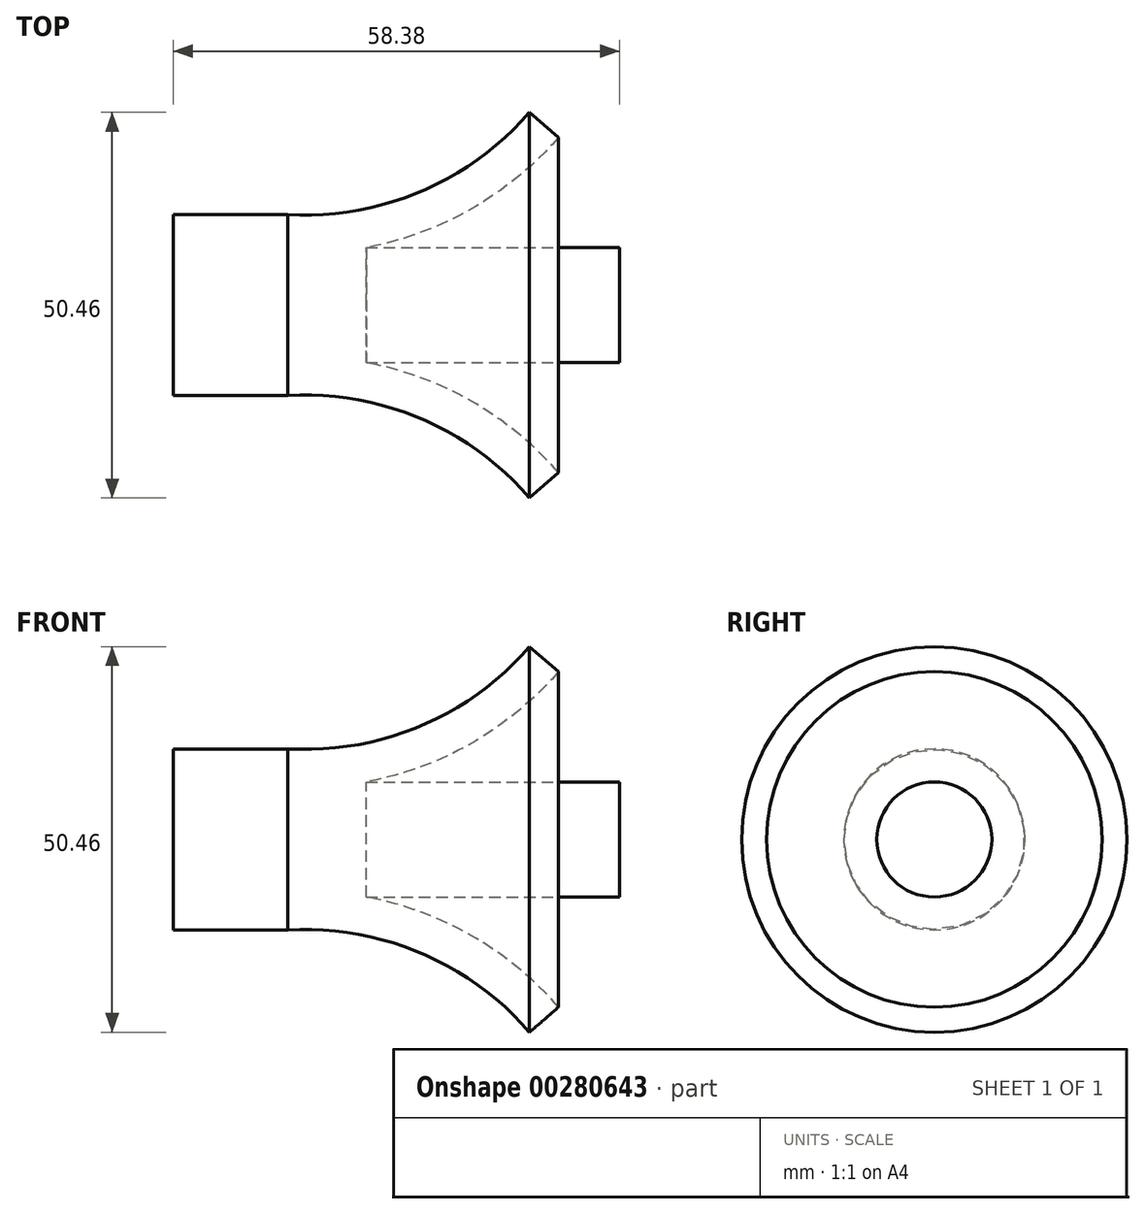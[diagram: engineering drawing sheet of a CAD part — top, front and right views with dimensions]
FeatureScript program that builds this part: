
annotation { "Feature Type Name" : "Feature", "Feature Type Description" : "" }
export const myFeature = defineFeature(function(context is Context, id is Id, definition is map)
    precondition{}
    {
        {
            var Q0;
            Q0=qCreatedBy(makeId("Top.planeOp"),FACE);
            var sketch = newSketch(context, id + "F0", { "sketchPlane" : qUnion([Q0])});
            skLineSegment(sketch, "E0", {"start": v(0, 0) * mm, "end": v(0, 11.86) * mm});
            skArc(sketch, "E1", {"start": v(0, 11.86) * mm, "mid": v(17.37, 14.86) * mm, "end": v(31.62, 25.23) * mm});
            skLineSegment(sketch, "E2", {"start": v(43.38, 2.53) * mm, "end": v(43.38, 0) * mm});
            skLineSegment(sketch, "E3", {"start": v(43.38, 0) * mm, "end": v(0, 0) * mm});
            skArc(sketch, "E4.0", {"start": v(-0.29, 6.86) * mm, "mid": v(-0.14, 6.86) * mm, "end": v(0, 6.85) * mm});
            skLineSegment(sketch, "E5.0", {"start": v(10.23, 7.53) * mm, "end": v(43.38, 7.53) * mm});
            skLineSegment(sketch, "E6", {"start": v(31.62, 25.23) * mm, "end": v(35.4, 21.96) * mm});
            skLineSegment(sketch, "E7", {"start": v(43.38, 7.53) * mm, "end": v(43.38, 2.53) * mm});
            skArc(sketch, "E8.trimOffspring", {"start": v(10.23, 7.53) * mm, "mid": v(24.04, 12.6) * mm, "end": v(35.4, 21.96) * mm});
            skSolve(sketch);
        }
        {
            var Q0;
            {var subQ0=sQuery(id+"F0.wireOp",EDGE,"E1");Q0=makeQuery(id+"F0.imprint","IMPRINT",FACE,{"disambiguationData":[TD([[makeQuery(id+"F0.imprint","IMPRINT",EDGE,{"derivedFrom":subQ0}),-1.0]])]});}
            var Q1;
            Q1=sQuery(id+"F0.wireOp",EDGE,"E3");
            revolve(context, id + "F1", {"entities" : qUnion([Q0]), "axis" : qUnion([Q1]), "revolveType" : RevolveType.FULL});
        }
        {
            var Q0;
            Q0=makeQuery(id+"F1.opRevolve","SWEPT_FACE",FACE,{"disambiguationData":[OSD([sQuery(id+"F0.wireOp",EDGE,"E0")])]});
            extrude(context, id + "F2", {"entities" : qUnion([Q0]), "operationType" : NewBodyOperationType.ADD, "depth" : 15 * mm});
        }
    });
